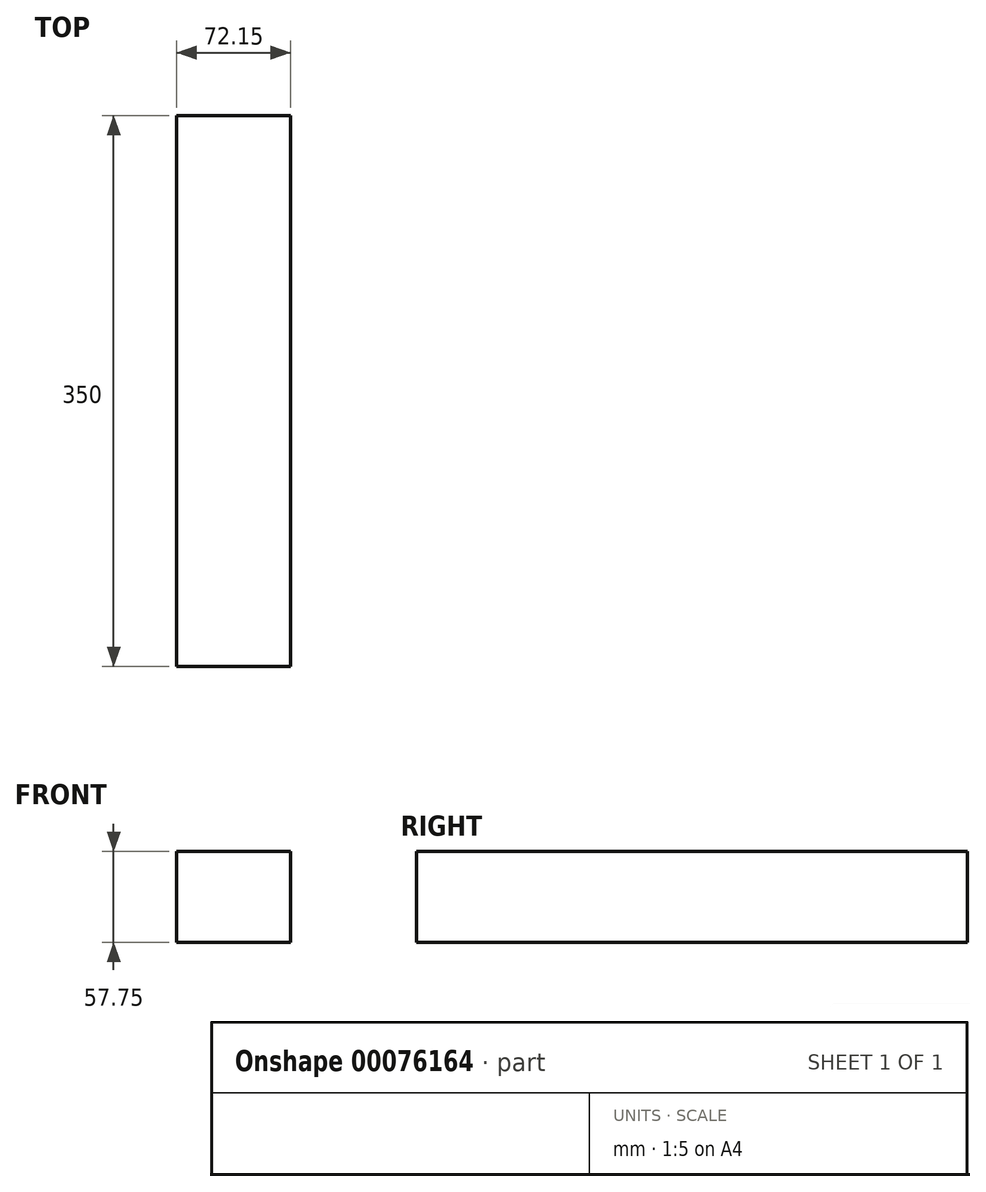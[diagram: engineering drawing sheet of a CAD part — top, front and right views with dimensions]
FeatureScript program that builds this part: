
annotation { "Feature Type Name" : "Feature", "Feature Type Description" : "" }
export const myFeature = defineFeature(function(context is Context, id is Id, definition is map)
    precondition{}
    {
        {
            var Q0;
            Q0=qCreatedBy(makeId("Front.planeOp"),FACE);
            var sketch = newSketch(context, id + "F0", { "sketchPlane" : qUnion([Q0])});
            skLineSegment(sketch, "E0", {"start": v(0, 0) * mm, "end": v(-72.15, 0) * mm});
            skLineSegment(sketch, "E1", {"start": v(-72.15, 0) * mm, "end": v(-72.15, 57.75) * mm});
            skLineSegment(sketch, "E2", {"start": v(-72.15, 57.75) * mm, "end": v(0, 57.75) * mm});
            skLineSegment(sketch, "E3", {"start": v(0, 57.75) * mm, "end": v(0, 0) * mm});
            skSolve(sketch);
        }
        {
            var Q0;
            Q0 = qSketchRegion(id + "F0", true);
            var Q1;
            Q1=makeQuery(id+"F0.imprint","IMPRINT",FACE,{"disambiguationData":[TD([[makeQuery(id+"F0.imprint","IMPRINT",EDGE,{"derivedFrom":sQuery(id+"F0.wireOp",EDGE,"E0")}),-1.0]])]});
            extrude(context, id + "F1", {"entities" : qUnion([Q0, Q1]), "oppositeDirection" : true, "depth" : 350 * mm});
        }
        {
            var Q0;
            Q0=makeQuery(id+"F1.opExtrude","SWEPT_FACE",FACE,{"disambiguationData":[OSD([sQuery(id+"F0.wireOp",EDGE,"E2")])]});
            var sketch = newSketch(context, id + "F2", { "sketchPlane" : qUnion([Q0])});
            skCircle(sketch, "E4", {"center": v(-36.07, 150) * mm, "radius": 25 * mm});
            skLineSegment(sketch, "E5", {"start": v(-36.07, 0) * mm, "end": v(-36.07, 350) * mm});
            skSolve(sketch);
        }
        {
            var Q0;
            Q0=sQuery(id+"F2.wireOp",EDGE,"E4");
            extrude(context, id + "F3", {"bodyType" : ToolBodyType.SURFACE, "surfaceEntities" : qUnion([Q0]), "depth" : 110.34 * mm});
        }
    });
